# Revit family: 20109_RFA
name_source: partatom
category: Aparatos sanitarios
units: mm (PartAtom-declared; Revit-internal decimal feet)

## family parameters
Activar corte en vistas = No
Compartido = No
Corte con vacíos al cargar = No
Cota de conector redondo = Usar diámetro
Mantener orientación de anotación = No
Número OmniClass = 23.45.00.00
Punto de cálculo de habitación = No
Se basa en plano de trabajo = No
Siempre vertical = Sí
Tipo de pieza = Normal
Título OmniClass = Sanitary, Laundry, and Cleaning Equipment

## types (1)
- 20109
    Alto = 3"
    Ancho = 9"
    Brass Chromed = Brass
    Comentarios de tipo = Accesories
    Descripción = Toallero Sencillo
    Elevación por defecto = 48"
    Fabricante = HELVEX
    Features = Toallero Sencillo que armoniza con la colección de la línea de accesorios Máxima..
Montaje oculto, no expone los tornillos de fijación.
Fácil de instalar.
    Imagen de tipo = 20109.png
    Largo = 10"
    Modelo = 20109
    URL = https://helvex.com.mx

## geometry (parser evidence)
native form markers: Sweep x3
no freeform markers — native parametric forms only
